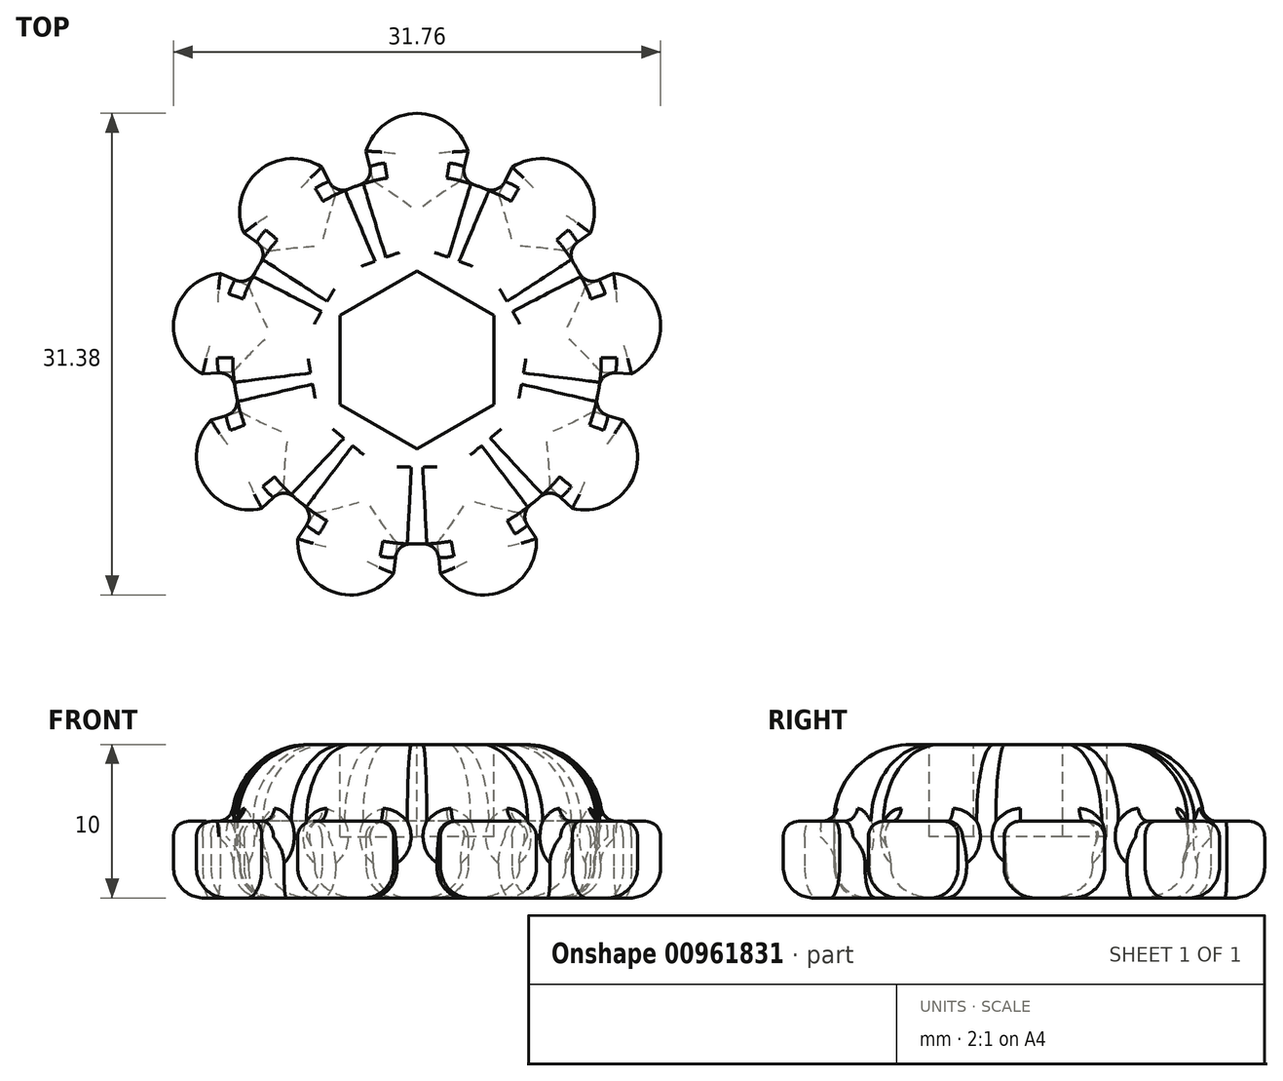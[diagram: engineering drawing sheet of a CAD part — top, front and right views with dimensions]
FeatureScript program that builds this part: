
annotation { "Feature Type Name" : "Feature", "Feature Type Description" : "" }
export const myFeature = defineFeature(function(context is Context, id is Id, definition is map)
    precondition{}
    {
        {
            var Q0;
            Q0=qCreatedBy(makeId("Top.planeOp"),FACE);
            var sketch = newSketch(context, id + "F0", { "sketchPlane" : qUnion([Q0])});
            skLineSegment(sketch, "E0", {"start": v(0, 0) * mm, "end": v(-3.32, 13.6) * mm});
            skLineSegment(sketch, "E1.MirrorCS", {"start": v(0, 0) * mm, "end": v(3.32, 13.6) * mm});
            skArc(sketch, "E2", {"start": v(3.32, 13.6) * mm, "mid": v(0, 16.07) * mm, "end": v(-3.32, 13.6) * mm});
            skArc(sketch, "E3.1.0", {"start": v(-6.2, 12.55) * mm, "mid": v(-10.33, 12.31) * mm, "end": v(-11.29, 8.28) * mm});
            skLineSegment(sketch, "E3.1.1", {"start": v(0, 0) * mm, "end": v(-11.29, 8.28) * mm});
            skLineSegment(sketch, "E3.1.2", {"start": v(0, 0) * mm, "end": v(-6.2, 12.55) * mm});
            skArc(sketch, "E3.2.0", {"start": v(-12.82, 5.64) * mm, "mid": v(-15.83, 2.8) * mm, "end": v(-13.97, -0.91) * mm});
            skLineSegment(sketch, "E3.2.1", {"start": v(0, 0) * mm, "end": v(-13.97, -0.91) * mm});
            skLineSegment(sketch, "E3.2.2", {"start": v(0, 0) * mm, "end": v(-12.82, 5.64) * mm});
            skArc(sketch, "E3.3.0", {"start": v(-13.44, -3.92) * mm, "mid": v(-13.92, -8.04) * mm, "end": v(-10.12, -9.68) * mm});
            skLineSegment(sketch, "E3.3.1", {"start": v(0, 0) * mm, "end": v(-10.12, -9.68) * mm});
            skLineSegment(sketch, "E3.3.2", {"start": v(0, 0) * mm, "end": v(-13.44, -3.92) * mm});
            skArc(sketch, "E3.4.0", {"start": v(-7.78, -11.64) * mm, "mid": v(-5.5, -15.1) * mm, "end": v(-1.53, -13.92) * mm});
            skLineSegment(sketch, "E3.4.1", {"start": v(0, 0) * mm, "end": v(-1.53, -13.92) * mm});
            skLineSegment(sketch, "E3.4.2", {"start": v(0, 0) * mm, "end": v(-7.78, -11.64) * mm});
            skArc(sketch, "E3.5.0", {"start": v(1.53, -13.92) * mm, "mid": v(5.5, -15.1) * mm, "end": v(7.78, -11.64) * mm});
            skLineSegment(sketch, "E3.5.1", {"start": v(0, 0) * mm, "end": v(7.78, -11.64) * mm});
            skLineSegment(sketch, "E3.5.2", {"start": v(0, 0) * mm, "end": v(1.53, -13.92) * mm});
            skArc(sketch, "E3.6.0", {"start": v(10.12, -9.68) * mm, "mid": v(13.92, -8.04) * mm, "end": v(13.44, -3.92) * mm});
            skLineSegment(sketch, "E3.6.1", {"start": v(0, 0) * mm, "end": v(13.44, -3.92) * mm});
            skLineSegment(sketch, "E3.6.2", {"start": v(0, 0) * mm, "end": v(10.12, -9.68) * mm});
            skArc(sketch, "E3.7.0", {"start": v(13.97, -0.91) * mm, "mid": v(15.83, 2.8) * mm, "end": v(12.82, 5.64) * mm});
            skLineSegment(sketch, "E3.7.1", {"start": v(0, 0) * mm, "end": v(12.82, 5.64) * mm});
            skLineSegment(sketch, "E3.7.2", {"start": v(0, 0) * mm, "end": v(13.97, -0.91) * mm});
            skArc(sketch, "E3.8.0", {"start": v(11.29, 8.28) * mm, "mid": v(10.33, 12.31) * mm, "end": v(6.2, 12.55) * mm});
            skLineSegment(sketch, "E3.8.1", {"start": v(0, 0) * mm, "end": v(6.2, 12.55) * mm});
            skLineSegment(sketch, "E3.8.2", {"start": v(0, 0) * mm, "end": v(11.29, 8.28) * mm});
            skPoint(sketch, "E3.center", {"position": v(0, 0) * mm});
            skSolve(sketch);
        }
        {
            var Q0;
            Q0=qCreatedBy(makeId("Top.planeOp"),FACE);
            var sketch = newSketch(context, id + "F1", { "sketchPlane" : qUnion([Q0])});
            skCircle(sketch, "E4", {"center": v(0, 0) * mm, "radius": 6 * mm});
            skCircle(sketch, "E5.0", {"center": v(0, 0) * mm, "radius": 12 * mm});
            skSolve(sketch);
        }
        {
            var Q0;
            Q0 = qSketchRegion(id + "F1", true);
            var Q1;
            Q1=makeQuery(id+"F1.imprint","IMPRINT",FACE,{"disambiguationData":[TD([[makeQuery(id+"F1.imprint","IMPRINT",EDGE,{"derivedFrom":sQuery(id+"F1.wireOp",EDGE,"E4")}),1.0]])]});
            extrude(context, id + "F2", {"entities" : qUnion([Q0, Q1]), "depth" : 10 * mm, "offsetDistance" : 25 * mm});
        }
        {
            var Q0;
            Q0 = qSketchRegion(id + "F0", true);
            extrude(context, id + "F3", {"entities" : qUnion([Q0]), "operationType" : NewBodyOperationType.ADD, "depth" : 5 * mm, "offsetDistance" : 25 * mm});
        }
        {
            var Q0;
            Q0=makeQuery(id+"F2.opExtrude","CAP_FACE",FACE,{"disambiguationData":[OSD([sQuery(id+"F1.wireOp",EDGE,"E5.0")])],"isStart":false});
            var sketch = newSketch(context, id + "F4", { "sketchPlane" : qUnion([Q0])});
            skCircle(sketch, "E6.cCircle", {"center": v(0, 0) * mm, "radius": 5.02 * mm, "construction": true});
            skLineSegment(sketch, "E6.0", {"start": v(5.02, -2.9) * mm, "end": v(0, -5.8) * mm});
            skLineSegment(sketch, "E6.1", {"start": v(0, -5.8) * mm, "end": v(-5.02, -2.9) * mm});
            skLineSegment(sketch, "E6.2", {"start": v(-5.02, -2.9) * mm, "end": v(-5.02, 2.9) * mm});
            skLineSegment(sketch, "E6.3", {"start": v(-5.02, 2.9) * mm, "end": v(0, 5.8) * mm});
            skLineSegment(sketch, "E6.4", {"start": v(0, 5.8) * mm, "end": v(5.02, 2.9) * mm});
            skLineSegment(sketch, "E6.5", {"start": v(5.02, 2.9) * mm, "end": v(5.02, -2.9) * mm});
            skPoint(sketch, "E6.0.midPoint", {"position": v(2.51, -4.35) * mm});
            skSolve(sketch);
        }
        {
            var Q0;
            Q0=makeQuery(id+"F4.imprint","IMPRINT",FACE,{"disambiguationData":[TD([[makeQuery(id+"F4.imprint","IMPRINT",EDGE,{"derivedFrom":sQuery(id+"F4.wireOp",EDGE,"E6.0")}),-1.0]])]});
            extrude(context, id + "F5", {"entities" : qUnion([Q0]), "operationType" : NewBodyOperationType.REMOVE, "oppositeDirection" : true, "depth" : 6 * mm, "offsetDistance" : 25 * mm});
        }
        {
            var Q0;
            Q0=makeQuery(id+"F3.boolean.opBoolean","MERGE",FACE,{"derivedFrom":[makeQuery(id+"F2.opExtrude","CAP_FACE",FACE,{"disambiguationData":[OSD([sQuery(id+"F1.wireOp",EDGE,"E5.0")])],"isStart":true}),makeQuery(id+"F3.opExtrude","CAP_FACE",FACE,{"disambiguationData":[OSD([sQuery(id+"F0.wireOp",EDGE,"E0"),sQuery(id+"F0.wireOp",EDGE,"E1.MirrorCS"),sQuery(id+"F0.wireOp",EDGE,"E2")])],"isStart":true}),makeQuery(id+"F3.opExtrude","CAP_FACE",FACE,{"disambiguationData":[OSD([sQuery(id+"F0.wireOp",EDGE,"E3.1.0"),sQuery(id+"F0.wireOp",EDGE,"E3.1.1"),sQuery(id+"F0.wireOp",EDGE,"E3.1.2")])],"isStart":true}),makeQuery(id+"F3.opExtrude","CAP_FACE",FACE,{"disambiguationData":[OSD([sQuery(id+"F0.wireOp",EDGE,"E3.2.0"),sQuery(id+"F0.wireOp",EDGE,"E3.2.1"),sQuery(id+"F0.wireOp",EDGE,"E3.2.2")])],"isStart":true}),makeQuery(id+"F3.opExtrude","CAP_FACE",FACE,{"disambiguationData":[OSD([sQuery(id+"F0.wireOp",EDGE,"E3.3.0"),sQuery(id+"F0.wireOp",EDGE,"E3.3.1"),sQuery(id+"F0.wireOp",EDGE,"E3.3.2")])],"isStart":true}),makeQuery(id+"F3.opExtrude","CAP_FACE",FACE,{"disambiguationData":[OSD([sQuery(id+"F0.wireOp",EDGE,"E3.4.0"),sQuery(id+"F0.wireOp",EDGE,"E3.4.1"),sQuery(id+"F0.wireOp",EDGE,"E3.4.2")])],"isStart":true}),makeQuery(id+"F3.opExtrude","CAP_FACE",FACE,{"disambiguationData":[OSD([sQuery(id+"F0.wireOp",EDGE,"E3.5.0"),sQuery(id+"F0.wireOp",EDGE,"E3.5.1"),sQuery(id+"F0.wireOp",EDGE,"E3.5.2")])],"isStart":true}),makeQuery(id+"F3.opExtrude","CAP_FACE",FACE,{"disambiguationData":[OSD([sQuery(id+"F0.wireOp",EDGE,"E3.6.0"),sQuery(id+"F0.wireOp",EDGE,"E3.6.1"),sQuery(id+"F0.wireOp",EDGE,"E3.6.2")])],"isStart":true}),makeQuery(id+"F3.opExtrude","CAP_FACE",FACE,{"disambiguationData":[OSD([sQuery(id+"F0.wireOp",EDGE,"E3.7.0"),sQuery(id+"F0.wireOp",EDGE,"E3.7.1"),sQuery(id+"F0.wireOp",EDGE,"E3.7.2")])],"isStart":true}),makeQuery(id+"F3.opExtrude","CAP_FACE",FACE,{"disambiguationData":[OSD([sQuery(id+"F0.wireOp",EDGE,"E3.8.0"),sQuery(id+"F0.wireOp",EDGE,"E3.8.1"),sQuery(id+"F0.wireOp",EDGE,"E3.8.2")])],"isStart":true})]});
            fillet(context, id + "F6", {"entities" : qUnion([Q0]), "radius" : 2 * mm, "tangentPropagation" : true, "allowEdgeOverflow" : false});
        }
        {
            var Q0;
            Q0=makeQuery(id+"F3.opExtrude","CAP_FACE",FACE,{"disambiguationData":[OSD([sQuery(id+"F0.wireOp",EDGE,"E3.4.0"),sQuery(id+"F0.wireOp",EDGE,"E3.4.1"),sQuery(id+"F0.wireOp",EDGE,"E3.4.2")])],"isStart":false});
            var Q1;
            Q1=makeQuery(id+"F3.opExtrude","CAP_FACE",FACE,{"disambiguationData":[OSD([sQuery(id+"F0.wireOp",EDGE,"E3.5.0"),sQuery(id+"F0.wireOp",EDGE,"E3.5.1"),sQuery(id+"F0.wireOp",EDGE,"E3.5.2")])],"isStart":false});
            var Q2;
            Q2=makeQuery(id+"F3.opExtrude","CAP_FACE",FACE,{"disambiguationData":[OSD([sQuery(id+"F0.wireOp",EDGE,"E3.6.0"),sQuery(id+"F0.wireOp",EDGE,"E3.6.1"),sQuery(id+"F0.wireOp",EDGE,"E3.6.2")])],"isStart":false});
            var Q3;
            Q3=makeQuery(id+"F3.opExtrude","CAP_FACE",FACE,{"disambiguationData":[OSD([sQuery(id+"F0.wireOp",EDGE,"E3.7.0"),sQuery(id+"F0.wireOp",EDGE,"E3.7.1"),sQuery(id+"F0.wireOp",EDGE,"E3.7.2")])],"isStart":false});
            var Q4;
            Q4=makeQuery(id+"F3.opExtrude","CAP_FACE",FACE,{"disambiguationData":[OSD([sQuery(id+"F0.wireOp",EDGE,"E3.8.0"),sQuery(id+"F0.wireOp",EDGE,"E3.8.1"),sQuery(id+"F0.wireOp",EDGE,"E3.8.2")])],"isStart":false});
            var Q5;
            Q5=makeQuery(id+"F3.opExtrude","CAP_FACE",FACE,{"disambiguationData":[OSD([sQuery(id+"F0.wireOp",EDGE,"E3.3.0"),sQuery(id+"F0.wireOp",EDGE,"E3.3.1"),sQuery(id+"F0.wireOp",EDGE,"E3.3.2")])],"isStart":false});
            var Q6;
            Q6=makeQuery(id+"F3.opExtrude","CAP_FACE",FACE,{"disambiguationData":[OSD([sQuery(id+"F0.wireOp",EDGE,"E3.2.0"),sQuery(id+"F0.wireOp",EDGE,"E3.2.1"),sQuery(id+"F0.wireOp",EDGE,"E3.2.2")])],"isStart":false});
            var Q7;
            Q7=makeQuery(id+"F3.opExtrude","CAP_FACE",FACE,{"disambiguationData":[OSD([sQuery(id+"F0.wireOp",EDGE,"E3.1.0"),sQuery(id+"F0.wireOp",EDGE,"E3.1.1"),sQuery(id+"F0.wireOp",EDGE,"E3.1.2")])],"isStart":false});
            var Q8;
            Q8=makeQuery(id+"F3.opExtrude","CAP_FACE",FACE,{"disambiguationData":[OSD([sQuery(id+"F0.wireOp",EDGE,"E0"),sQuery(id+"F0.wireOp",EDGE,"E1.MirrorCS"),sQuery(id+"F0.wireOp",EDGE,"E2")])],"isStart":false});
            fillet(context, id + "F7", {"entities" : qUnion([Q0, Q1, Q2, Q3, Q4, Q5, Q6, Q7, Q8]), "radius" : 1 * mm, "tangentPropagation" : true, "allowEdgeOverflow" : false});
        }
        {
            var Q0;
            Q0=makeQuery(id+"F2.opExtrude","CAP_EDGE",EDGE,{"disambiguationData":[OSD([sQuery(id+"F1.wireOp",EDGE,"E5.0")])],"isStart":false});
            fillet(context, id + "F8", {"entities" : qUnion([Q0]), "radius" : 5 * mm, "tangentPropagation" : true, "allowEdgeOverflow" : false});
        }
    });
